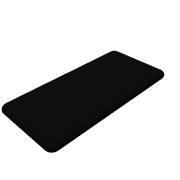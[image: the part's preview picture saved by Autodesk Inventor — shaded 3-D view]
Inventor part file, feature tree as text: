
AUTODESK INVENTOR PART (.ipt)
format: ipt  version: 2019 (Build 230136000, 136)  size: 173,568 bytes
history: native  units: mm
features: extrude x3, sketch x3, fillet x1, projected_geometry x1
ambient origin geometry x8: Origin, YZ Plane, XZ Plane, XY Plane, X Axis, Y Axis, Z Axis, Center Point
bodies: Solid1 (feature_tree)
feature tree (8):
  extrude  "Extrusion1"  Depth=8.63mm
  extrude  "Extrusion2"  Depth=0.5mm TaperAngle=0.0deg
  fillet  "Fillet1"  Radius=73.88mm
  extrude  "Extrusion3"  Depth=7.5mm
  sketch  "Sketch1"  dims[d0=8.63mm d1=11.5mm]
  sketch  "Sketch2"  dims[d2=11.0mm d3=0.5mm d4=0.0mm d5=73.88mm]
  projected_geometry  "Projected Loop1"
  sketch  "Sketch3"  dims[d6=155.0mm d7=33.5mm d8=12.5mm d9=7.5mm d10=8.15mm d11=0.0mm d12=4.0mm d13=20.0mm d14=2.0mm d15=0.75mm d16=0.0mm d17=9.0mm d18=2.0mm d19=29.0mm d20=7.5mm]
